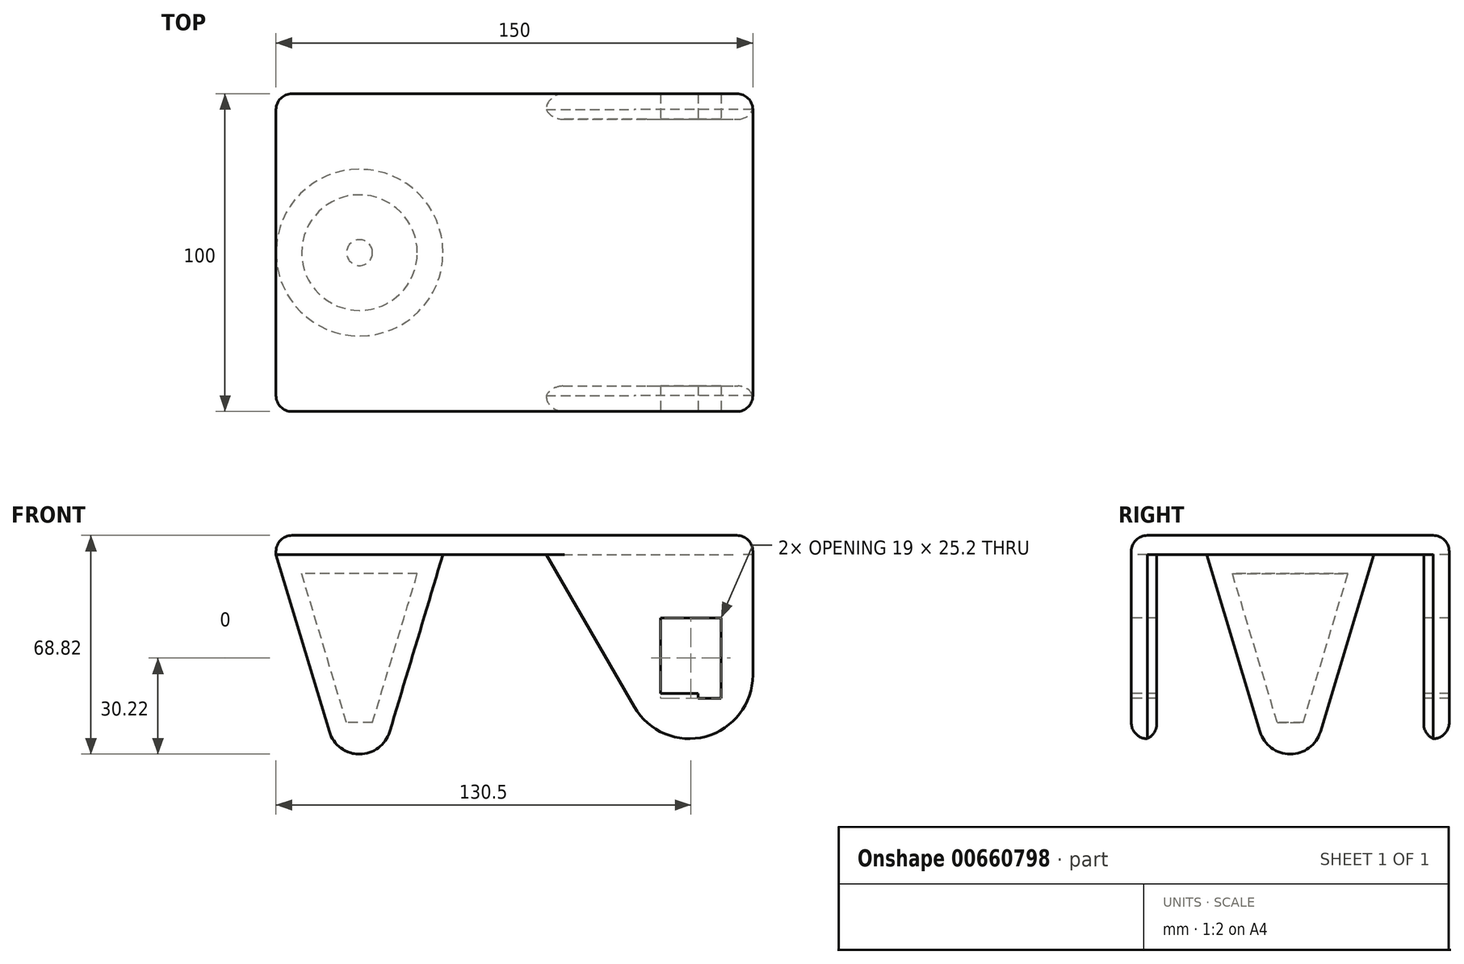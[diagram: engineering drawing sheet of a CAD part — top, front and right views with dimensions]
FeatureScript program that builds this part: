
annotation { "Feature Type Name" : "Feature", "Feature Type Description" : "" }
export const myFeature = defineFeature(function(context is Context, id is Id, definition is map)
    precondition{}
    {
        {
            var Q0;
            Q0=qCreatedBy(makeId("Top.planeOp"),FACE);
            var sketch = newSketch(context, id + "F0", { "sketchPlane" : qUnion([Q0])});
            skLineSegment(sketch, "E0.bottom", {"start": v(-75, 50) * mm, "end": v(75, 50) * mm});
            skLineSegment(sketch, "E0.top", {"start": v(-75, -50) * mm, "end": v(75, -50) * mm});
            skLineSegment(sketch, "E0.left", {"start": v(-75, 50) * mm, "end": v(-75, -50) * mm});
            skLineSegment(sketch, "E0.right", {"start": v(75, 50) * mm, "end": v(75, -50) * mm});
            skPoint(sketch, "E0.middle", {"position": v(0, 0) * mm});
            skSolve(sketch);
        }
        {
            var Q0;
            Q0=makeQuery(id+"F0.imprint","IMPRINT",FACE,{"disambiguationData":[TD([[makeQuery(id+"F0.imprint","IMPRINT",EDGE,{"derivedFrom":sQuery(id+"F0.wireOp",EDGE,"E0.bottom")}),-1.0]])]});
            extrude(context, id + "F1", {"entities" : qUnion([Q0]), "depth" : 6 * mm, "offsetDistance" : 25.4 * mm});
        }
        {
            var Q0;
            Q0=makeQuery(id+"F1.opExtrude","SWEPT_FACE",FACE,{"disambiguationData":[OSD([sQuery(id+"F0.wireOp",EDGE,"E0.top")])]});
            var sketch = newSketch(context, id + "F2", { "sketchPlane" : qUnion([Q0])});
            skLineSegment(sketch, "E1", {"start": v(65, -20) * mm, "end": v(46, -20) * mm});
            skLineSegment(sketch, "E2", {"start": v(10, 0) * mm, "end": v(75, 0) * mm});
            skLineSegment(sketch, "E3", {"start": v(75, 0) * mm, "end": v(75, -37.94) * mm});
            skLineSegment(sketch, "E4", {"start": v(10, 0) * mm, "end": v(37.68, -47.94) * mm});
            skArc(sketch, "E5.filletArc", {"start": v(37.68, -47.94) * mm, "mid": v(60.18, -57.26) * mm, "end": v(75, -37.94) * mm});
            skLineSegment(sketch, "E6.MirrorCS", {"start": v(57.8, -43.7) * mm, "end": v(57.8, -45.2) * mm});
            skLineSegment(sketch, "E7.MirrorCS", {"start": v(46, -43.7) * mm, "end": v(57.8, -43.7) * mm});
            skLineSegment(sketch, "E8.MirrorCS", {"start": v(46, -43.7) * mm, "end": v(46, -20) * mm});
            skLineSegment(sketch, "E9.MirrorCS", {"start": v(65, -45.2) * mm, "end": v(65, -20) * mm});
            skLineSegment(sketch, "E10.MirrorCS", {"start": v(57.8, -45.2) * mm, "end": v(65, -45.2) * mm});
            skSolve(sketch);
        }
        {
            var Q0;
            Q0=qCreatedBy(makeId("Top.planeOp"),FACE);
            var sketch = newSketch(context, id + "F3", { "sketchPlane" : qUnion([Q0])});
            skLineSegment(sketch, "E11.bottom", {"start": v(-60.46, 42) * mm, "end": v(110.6, 42) * mm});
            skLineSegment(sketch, "E11.top", {"start": v(-60.46, -42) * mm, "end": v(110.6, -42) * mm});
            skLineSegment(sketch, "E11.left", {"start": v(-60.46, 42) * mm, "end": v(-60.46, -42) * mm});
            skLineSegment(sketch, "E11.right", {"start": v(110.6, 42) * mm, "end": v(110.6, -42) * mm});
            skSolve(sketch);
        }
        {
            var Q0;
            Q0=qCreatedBy(makeId("Front.planeOp"),FACE);
            var sketch = newSketch(context, id + "F4", { "sketchPlane" : qUnion([Q0])});
            skLineSegment(sketch, "E12", {"start": v(-75, 0) * mm, "end": v(-48.74, 0) * mm});
            skLineSegment(sketch, "E13", {"start": v(-48.74, 0) * mm, "end": v(-48.74, -87.3) * mm});
            skLineSegment(sketch, "E14", {"start": v(-48.74, -87.3) * mm, "end": v(-75, 0) * mm});
            skCircle(sketch, "E15", {"center": v(-48.74, -52.92) * mm, "radius": 9.9 * mm});
            skLineSegment(sketch, "E16", {"start": v(-48.74, -6) * mm, "end": v(-66.93, -6) * mm});
            skLineSegment(sketch, "E17", {"start": v(-66.93, -6) * mm, "end": v(-52.82, -52.92) * mm});
            skLineSegment(sketch, "E18", {"start": v(-52.82, -52.92) * mm, "end": v(-48.74, -52.92) * mm});
            skLineSegment(sketch, "E19", {"start": v(-48.74, -62.82) * mm, "end": v(75.33, -62.82) * mm});
            skCircle(sketch, "E20", {"center": v(55.77, -39.7) * mm, "radius": 23.12 * mm});
            skSolve(sketch);
        }
        {
            var Q0;
            Q0=makeQuery(id+"F2.imprint","IMPRINT",FACE,{"disambiguationData":[TD([[makeQuery(id+"F2.imprint","IMPRINT",EDGE,{"derivedFrom":sQuery(id+"F2.wireOp",EDGE,"E1")}),-1.0]])]});
            extrude(context, id + "F5", {"entities" : qUnion([Q0]), "oppositeDirection" : true, "depth" : 100 * mm, "offsetDistance" : 25 * mm});
        }
        {
            var Q0;
            Q0=makeQuery(id+"F3.imprint","IMPRINT",FACE,{"disambiguationData":[TD([[makeQuery(id+"F3.imprint","IMPRINT",EDGE,{"derivedFrom":sQuery(id+"F3.wireOp",EDGE,"E11.bottom")}),-1.0]])]});
            extrude(context, id + "F6", {"entities" : qUnion([Q0]), "operationType" : NewBodyOperationType.REMOVE, "oppositeDirection" : true, "depth" : 200 * mm, "offsetDistance" : 25 * mm});
        }
        {
            var Q0;
            Q0=makeQuery(id+"F1.opExtrude","SWEPT_BODY",BODY,{"disambiguationData":[OSD([sQuery(id+"F0.wireOp",EDGE,"E0.bottom"),sQuery(id+"F0.wireOp",EDGE,"E0.top"),sQuery(id+"F0.wireOp",EDGE,"E0.left"),sQuery(id+"F0.wireOp",EDGE,"E0.right")])]});
            var Q1;
            Q1=makeQuery(id+"F6.boolean.opBoolean","SPLIT",BODY,{"disambiguationData":[OD(0.0)],"derivedFrom":makeQuery(id+"F5.opExtrude","SWEPT_BODY",BODY,{"disambiguationData":[OSD([sQuery(id+"F2.wireOp",EDGE,"E1"),sQuery(id+"F2.wireOp",EDGE,"E2"),sQuery(id+"F2.wireOp",EDGE,"E3"),sQuery(id+"F2.wireOp",EDGE,"E4"),sQuery(id+"F2.wireOp",EDGE,"E5.filletArc"),sQuery(id+"F2.wireOp",EDGE,"E6.MirrorCS"),sQuery(id+"F2.wireOp",EDGE,"E7.MirrorCS"),sQuery(id+"F2.wireOp",EDGE,"E8.MirrorCS"),sQuery(id+"F2.wireOp",EDGE,"E9.MirrorCS"),sQuery(id+"F2.wireOp",EDGE,"E10.MirrorCS")])]})});
            var Q2;
            Q2=makeQuery(id+"F6.boolean.opBoolean","SPLIT",BODY,{"disambiguationData":[OD(1.0)],"derivedFrom":makeQuery(id+"F5.opExtrude","SWEPT_BODY",BODY,{"disambiguationData":[OSD([sQuery(id+"F2.wireOp",EDGE,"E1"),sQuery(id+"F2.wireOp",EDGE,"E2"),sQuery(id+"F2.wireOp",EDGE,"E3"),sQuery(id+"F2.wireOp",EDGE,"E4"),sQuery(id+"F2.wireOp",EDGE,"E5.filletArc"),sQuery(id+"F2.wireOp",EDGE,"E6.MirrorCS"),sQuery(id+"F2.wireOp",EDGE,"E7.MirrorCS"),sQuery(id+"F2.wireOp",EDGE,"E8.MirrorCS"),sQuery(id+"F2.wireOp",EDGE,"E9.MirrorCS"),sQuery(id+"F2.wireOp",EDGE,"E10.MirrorCS")])]})});
            booleanBodies(context, id + "F7", {"operationType" : BooleanOperationType.UNION, "tools" : qUnion([Q0, Q1, Q2])});
        }
        {
            var Q0;
            {var subQ5=sQuery(id+"F4.wireOp",EDGE,"E12");Q0=makeQuery(id+"F4.imprint","IMPRINT",FACE,{"disambiguationData":[TD([[makeQuery(id+"F4.imprint","IMPRINT",EDGE,{"derivedFrom":subQ5}),-1.0]])]});}
            var Q1;
            {var subQ4=sQuery(id+"F4.wireOp",EDGE,"E18");Q1=makeQuery(id+"F4.imprint","IMPRINT",FACE,{"disambiguationData":[TD([[makeQuery(id+"F4.imprint","IMPRINT",EDGE,{"derivedFrom":subQ4}),-1.0]])]});}
            var Q2;
            Q2=sQuery(id+"F4.wireOp",EDGE,"E13");
            revolve(context, id + "F8", {"operationType" : NewBodyOperationType.ADD, "entities" : qUnion([Q0, Q1]), "axis" : qUnion([Q2]), "revolveType" : RevolveType.FULL});
        }
        {
            var Q0;
            Q0=makeQuery(id+"F1.opExtrude","CAP_FACE",FACE,{"disambiguationData":[OSD([sQuery(id+"F0.wireOp",EDGE,"E0.bottom"),sQuery(id+"F0.wireOp",EDGE,"E0.top"),sQuery(id+"F0.wireOp",EDGE,"E0.left"),sQuery(id+"F0.wireOp",EDGE,"E0.right")])],"isStart":false});
            var Q1;
            Q1=makeQuery(id+"F7.opBoolean","MERGE",EDGE,{"derivedFrom":[makeQuery(id+"F1.opExtrude","SWEPT_EDGE",EDGE,{"disambiguationData":[OSD([sQuery(id+"F0.wireOp",EDGE,"E0.bottom"),sQuery(id+"F0.wireOp",EDGE,"E0.right")])]}),makeQuery(id+"F5.opExtrude","CAP_EDGE",EDGE,{"disambiguationData":[OSD([sQuery(id+"F2.wireOp",EDGE,"E3")])],"isStart":false})]});
            var Q2;
            Q2=makeQuery(id+"F1.opExtrude","SWEPT_EDGE",EDGE,{"disambiguationData":[OSD([sQuery(id+"F0.wireOp",EDGE,"E0.bottom"),sQuery(id+"F0.wireOp",EDGE,"E0.left")])]});
            var Q3;
            Q3=makeQuery(id+"F7.opBoolean","MERGE",EDGE,{"derivedFrom":[makeQuery(id+"F1.opExtrude","SWEPT_EDGE",EDGE,{"disambiguationData":[OSD([sQuery(id+"F0.wireOp",EDGE,"E0.top"),sQuery(id+"F0.wireOp",EDGE,"E0.right")])]}),makeQuery(id+"F5.opExtrude","CAP_EDGE",EDGE,{"disambiguationData":[OSD([sQuery(id+"F2.wireOp",EDGE,"E3")])],"isStart":true})]});
            var Q4;
            Q4=makeQuery(id+"F1.opExtrude","SWEPT_EDGE",EDGE,{"disambiguationData":[OSD([sQuery(id+"F0.wireOp",EDGE,"E0.top"),sQuery(id+"F0.wireOp",EDGE,"E0.left")])]});
            fillet(context, id + "F9", {"entities" : qUnion([Q0, Q1, Q2, Q3, Q4]), "radius" : 5 * mm, "tangentPropagation" : true, "allowEdgeOverflow" : false});
        }
        {
            var Q0;
            Q0=makeQuery(id+"F6.boolean.opBoolean","INTERSECT",EDGE,{"derivedFrom":[makeQuery(id+"F5.opExtrude","SWEPT_FACE",FACE,{"disambiguationData":[OSD([sQuery(id+"F2.wireOp",EDGE,"E3")])]}),makeQuery(id+"F6.opExtrude","SWEPT_FACE",FACE,{"disambiguationData":[OSD([sQuery(id+"F3.wireOp",EDGE,"E11.bottom")])]})]});
            var Q1;
            Q1=makeQuery(id+"F6.boolean.opBoolean","INTERSECT",EDGE,{"derivedFrom":[makeQuery(id+"F5.opExtrude","SWEPT_FACE",FACE,{"disambiguationData":[OSD([sQuery(id+"F2.wireOp",EDGE,"E5.filletArc")])]}),makeQuery(id+"F6.opExtrude","SWEPT_FACE",FACE,{"disambiguationData":[OSD([sQuery(id+"F3.wireOp",EDGE,"E11.top")])]})]});
            fillet(context, id + "F10", {"entities" : qUnion([Q0, Q1]), "radius" : 5 * mm, "tangentPropagation" : true, "allowEdgeOverflow" : false});
        }
    });
